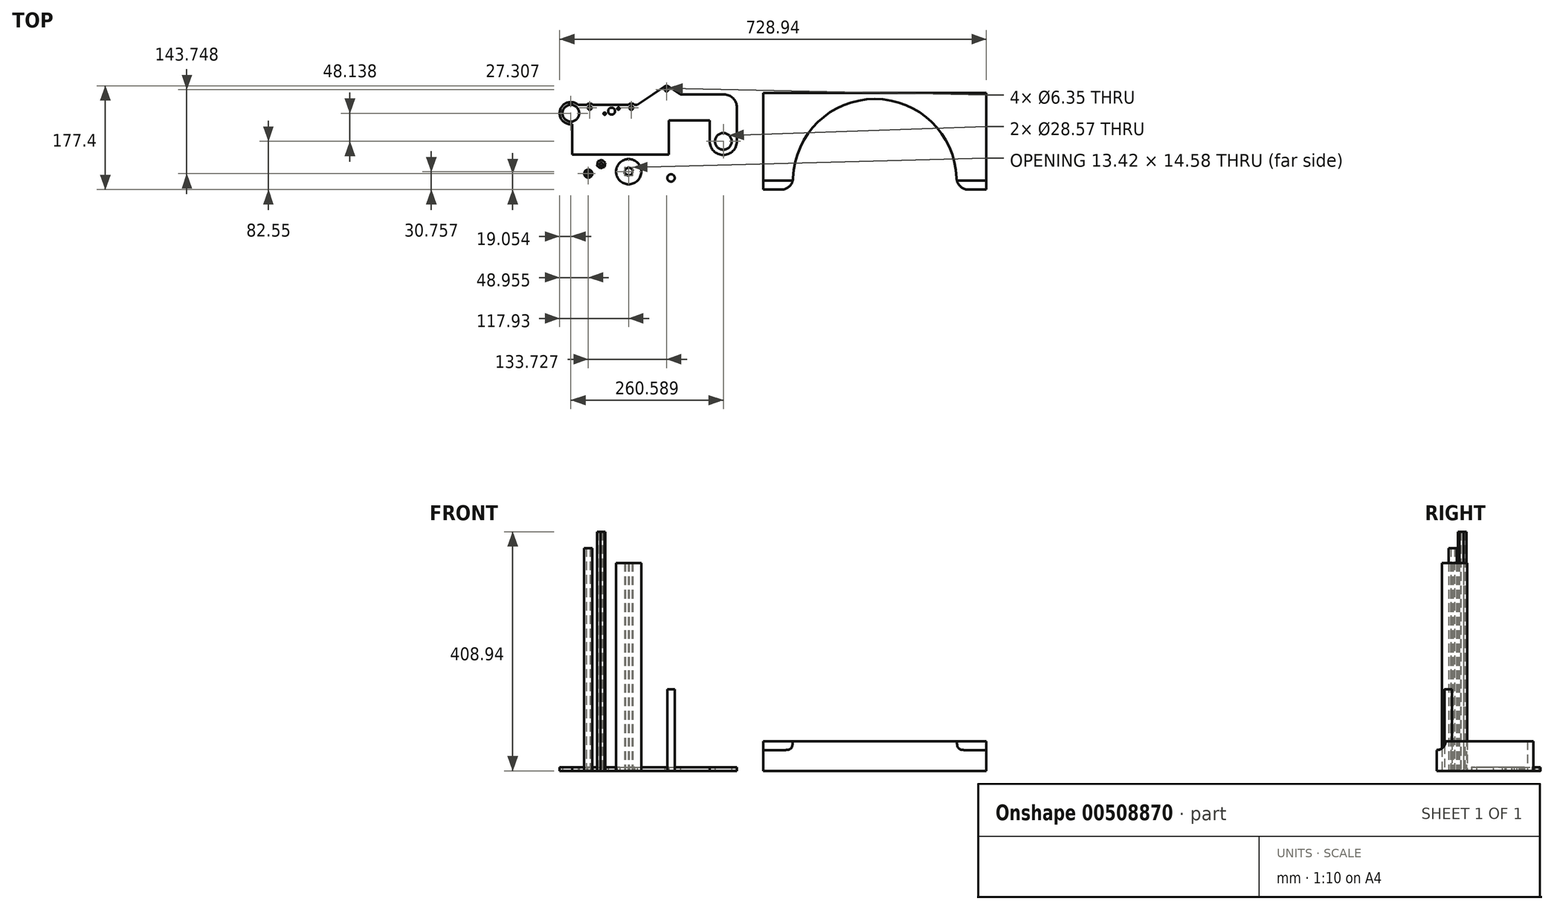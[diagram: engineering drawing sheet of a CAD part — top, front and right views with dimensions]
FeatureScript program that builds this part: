
annotation { "Feature Type Name" : "Feature", "Feature Type Description" : "" }
export const myFeature = defineFeature(function(context is Context, id is Id, definition is map)
    precondition{}
    {
        {
            assignVariable(context, id + "F0", {"name" : "inner_width", "anyValue" : 381 * mm});
        }
        {
            var Q0;
            Q0=qCreatedBy(makeId("Top.planeOp"),FACE);
            var sketch = newSketch(context, id + "F1", { "sketchPlane" : qUnion([Q0])});
            skCircle(sketch, "E0", {"center": v(-76.69, 48.14) * mm, "radius": 21.59 * mm, "construction": true});
            skCircle(sketch, "E1", {"center": v(-76.69, 48.14) * mm, "radius": 14.29 * mm});
            skArc(sketch, "E2", {"start": v(-63.83, 62.2) * mm, "mid": v(-94.85, 53.87) * mm, "end": v(-74.22, 29.25) * mm});
            skLineSegment(sketch, "E3", {"start": v(-74.22, 29.25) * mm, "end": v(-74.22, -22.94) * mm});
            skLineSegment(sketch, "E4", {"start": v(-74.22, -22.94) * mm, "end": v(90.88, -22.94) * mm});
            skLineSegment(sketch, "E5", {"start": v(90.88, -22.94) * mm, "end": v(90.88, 35.73) * mm});
            skLineSegment(sketch, "E6", {"start": v(184.86, 80.18) * mm, "end": v(110.56, 80.18) * mm});
            skLineSegment(sketch, "E7", {"start": v(-74.22, 14.56) * mm, "end": v(90.88, 14.56) * mm, "construction": true});
            skPoint(sketch, "E8.centerSnap0", {"position": v(205.18, 57.96) * mm});
            skArc(sketch, "E9", {"start": v(90.5, 93.76) * mm, "mid": v(86.94, 94.85) * mm, "end": v(83.38, 93.76) * mm});
            skLineSegment(sketch, "E10", {"start": v(83.38, 93.76) * mm, "end": v(63.33, 80.18) * mm});
            skLineSegment(sketch, "E11", {"start": v(90.5, 93.76) * mm, "end": v(110.56, 80.18) * mm});
            skCircle(sketch, "E12", {"center": v(86.94, 88.5) * mm, "radius": 3.18 * mm});
            skLineSegment(sketch, "E13", {"start": v(36.9, 62.2) * mm, "end": v(63.33, 80.18) * mm});
            skCircle(sketch, "E14", {"center": v(-7, 51.68) * mm, "radius": 6 * mm});
            skCircle(sketch, "E15", {"center": v(4.74, 55.96) * mm, "radius": 2 * mm});
            skLineSegment(sketch, "E16", {"start": v(4.74, 55.96) * mm, "end": v(-18.75, 47.4) * mm, "construction": true});
            skCircle(sketch, "E17", {"center": v(-18.75, 47.4) * mm, "radius": 2 * mm});
            skLineSegment(sketch, "E18", {"start": v(-7, 51.68) * mm, "end": v(3.74, 51.68) * mm, "construction": true});
            skCircle(sketch, "E19", {"center": v(-44.31, 57.12) * mm, "radius": 3.18 * mm});
            skCircle(sketch, "E20", {"center": v(26.72, 57.12) * mm, "radius": 3.18 * mm});
            skLineSegment(sketch, "E21", {"start": v(-63.83, 62.2) * mm, "end": v(-50, 62.2) * mm});
            skArc(sketch, "E22", {"start": v(-38.63, 62.2) * mm, "mid": v(-44.31, 64.74) * mm, "end": v(-50, 62.2) * mm});
            skArc(sketch, "E23", {"start": v(32.4, 62.2) * mm, "mid": v(26.72, 64.74) * mm, "end": v(21.04, 62.2) * mm});
            skLineSegment(sketch, "E24.trimOffspring", {"start": v(32.4, 62.2) * mm, "end": v(36.9, 62.2) * mm});
            skLineSegment(sketch, "E25.trimOffspring", {"start": v(-38.63, 62.2) * mm, "end": v(21.04, 62.2) * mm});
            skPoint(sketch, "E26.orphan", {"position": v(205.18, 35.73) * mm});
            skPoint(sketch, "E27.end.orphan", {"position": v(205.18, 80.18) * mm});
            skLineSegment(sketch, "E28", {"start": v(160.73, 35.73) * mm, "end": v(160.73, 0) * mm});
            skArc(sketch, "E29", {"start": v(184.86, 80.18) * mm, "mid": v(200.57, 73.67) * mm, "end": v(207.08, 57.96) * mm});
            skLineSegment(sketch, "E30", {"start": v(207.08, 57.96) * mm, "end": v(207.08, 0) * mm});
            skArc(sketch, "E31", {"start": v(160.73, 0) * mm, "mid": v(183.9, -23.18) * mm, "end": v(207.08, 0) * mm});
            skLineSegment(sketch, "E32", {"start": v(90.88, 35.73) * mm, "end": v(160.73, 35.73) * mm});
            skCircle(sketch, "E33", {"center": v(183.9, 0) * mm, "radius": 14.29 * mm});
            skSolve(sketch);
        }
        {
            var Q0;
            Q0=makeQuery(id+"F1.imprint","IMPRINT",FACE,{"disambiguationData":[TD([[makeQuery(id+"F1.imprint","IMPRINT",EDGE,{"derivedFrom":sQuery(id+"F1.wireOp",EDGE,"E1")}),-1.0]])]});
            var Q1;
            Q1=makeQuery(id+"F1.imprint","IMPRINT",FACE,{"disambiguationData":[TD([[makeQuery(id+"F1.imprint","IMPRINT",EDGE,{"derivedFrom":sQuery(id+"F1.wireOp",EDGE,"E19")}),-1.0]])]});
            var Q2;
            Q2=makeQuery(id+"F1.imprint","IMPRINT",FACE,{"disambiguationData":[TD([[makeQuery(id+"F1.imprint","IMPRINT",EDGE,{"derivedFrom":sQuery(id+"F1.wireOp",EDGE,"E20")}),-1.0]])]});
            extrude(context, id + "F2", {"entities" : qUnion([Q0, Q1, Q2]), "depth" : 6.35 * mm});
        }
        {
            var Q0;
            Q0=qCreatedBy(makeId("Top.planeOp"),FACE);
            var sketch = newSketch(context, id + "F3", { "sketchPlane" : qUnion([Q0])});
            skCircle(sketch, "E34", {"center": v(-46.78, -55.24) * mm, "radius": 6.99 * mm});
            skCircle(sketch, "E35", {"center": v(-46.78, -55.24) * mm, "radius": 3.18 * mm});
            skSolve(sketch);
        }
        {
            var Q0;
            Q0=qSketchRegion(id+"F3",true);
            extrude(context, id + "F4", {"entities" : qUnion([Q0]), "depth" : getVariable(context, 'inner_width')});
        }
        {
            var Q0;
            Q0=qCreatedBy(makeId("Top.planeOp"),FACE);
            var sketch = newSketch(context, id + "F5", { "sketchPlane" : qUnion([Q0])});
            skCircle(sketch, "E36.cCircle", {"center": v(-24.83, -39.03) * mm, "radius": 6.35 * mm, "construction": true});
            skLineSegment(sketch, "E36.0", {"start": v(-19.3, -43.86) * mm, "end": v(-26.24, -46.23) * mm});
            skLineSegment(sketch, "E36.1", {"start": v(-26.24, -46.23) * mm, "end": v(-31.77, -41.4) * mm});
            skLineSegment(sketch, "E36.2", {"start": v(-31.77, -41.4) * mm, "end": v(-30.35, -34.2) * mm});
            skLineSegment(sketch, "E36.3", {"start": v(-30.35, -34.2) * mm, "end": v(-23.4, -31.84) * mm});
            skLineSegment(sketch, "E36.4", {"start": v(-23.4, -31.84) * mm, "end": v(-17.89, -36.66) * mm});
            skLineSegment(sketch, "E36.5", {"start": v(-17.89, -36.66) * mm, "end": v(-19.3, -43.86) * mm});
            skPoint(sketch, "E36.0.midPoint", {"position": v(-22.77, -45.04) * mm});
            skCircle(sketch, "E37", {"center": v(-24.83, -39.03) * mm, "radius": 2.55 * mm});
            skSolve(sketch);
        }
        {
            var Q0;
            Q0=qSketchRegion(id+"F5",true);
            extrude(context, id + "F6", {"entities" : qUnion([Q0]), "depth" : getVariable(context, 'inner_width') + 27.94 * mm});
        }
        {
            var Q0;
            Q0=qCreatedBy(makeId("Top.planeOp"),FACE);
            var sketch = newSketch(context, id + "F7", { "sketchPlane" : qUnion([Q0])});
            skCircle(sketch, "E38", {"center": v(22.2, -51.8) * mm, "radius": 21.59 * mm});
            skCircle(sketch, "E39.cCircle", {"center": v(22.2, -51.8) * mm, "radius": 6.35 * mm, "construction": true});
            skLineSegment(sketch, "E39.0", {"start": v(28.1, -56.12) * mm, "end": v(21.4, -59.08) * mm});
            skLineSegment(sketch, "E39.1", {"start": v(21.4, -59.08) * mm, "end": v(15.48, -54.75) * mm});
            skLineSegment(sketch, "E39.2", {"start": v(15.48, -54.75) * mm, "end": v(16.27, -47.46) * mm});
            skLineSegment(sketch, "E39.3", {"start": v(16.27, -47.46) * mm, "end": v(22.98, -44.5) * mm});
            skLineSegment(sketch, "E39.4", {"start": v(22.98, -44.5) * mm, "end": v(28.9, -48.83) * mm});
            skLineSegment(sketch, "E39.5", {"start": v(28.9, -48.83) * mm, "end": v(28.1, -56.12) * mm});
            skPoint(sketch, "E39.0.midPoint", {"position": v(24.75, -57.6) * mm});
            skSolve(sketch);
        }
        {
            var Q0;
            Q0=makeQuery(id+"F7.imprint","IMPRINT",FACE,{"disambiguationData":[TD([[makeQuery(id+"F7.imprint","IMPRINT",EDGE,{"derivedFrom":sQuery(id+"F7.wireOp",EDGE,"E38")}),1.0]])]});
            extrude(context, id + "F8", {"entities" : qUnion([Q0]), "depth" : getVariable(context, 'inner_width') - 25.4 * mm});
        }
        {
            var Q0;
            Q0=qCreatedBy(makeId("Top.planeOp"),FACE);
            var sketch = newSketch(context, id + "F9", { "sketchPlane" : qUnion([Q0])});
            skLineSegment(sketch, "E40.bottom", {"start": v(252.2, 82.55) * mm, "end": v(633.2, 82.55) * mm});
            skLineSegment(sketch, "E40.top", {"start": v(252.2, -82.55) * mm, "end": v(303.84, -82.55) * mm});
            skLineSegment(sketch, "E40.left", {"start": v(252.2, 82.55) * mm, "end": v(252.2, -82.55) * mm});
            skLineSegment(sketch, "E40.right", {"start": v(633.2, 82.55) * mm, "end": v(633.2, -82.55) * mm});
            skPoint(sketch, "E40.middle", {"position": v(442.7, 0) * mm});
            skArc(sketch, "E41", {"start": v(581.57, -82.55) * mm, "mid": v(442.7, 72.4) * mm, "end": v(303.84, -82.55) * mm});
            skLineSegment(sketch, "E42.trimOffspring", {"start": v(581.57, -82.55) * mm, "end": v(633.2, -82.55) * mm});
            skSolve(sketch);
        }
        {
            var Q0;
            Q0=qSketchRegion(id+"F9",true);
            extrude(context, id + "F10", {"entities" : qUnion([Q0]), "depth" : 50.8 * mm});
        }
        {
            var Q0;
            Q0=makeQuery(id+"F10.opExtrude","SWEPT_EDGE",EDGE,{"disambiguationData":[OSD([sQuery(id+"F9.wireOp",EDGE,"E40.top"),sQuery(id+"F9.wireOp",EDGE,"E41")])]});
            var Q1;
            Q1=makeQuery(id+"F10.opExtrude","SWEPT_EDGE",EDGE,{"disambiguationData":[OSD([sQuery(id+"F9.wireOp",EDGE,"E41"),sQuery(id+"F9.wireOp",EDGE,"E42.trimOffspring")])]});
            fillet(context, id + "F11", {"entities" : qUnion([Q0, Q1]), "radius" : 20.32 * mm, "tangentPropagation" : true, "allowEdgeOverflow" : false});
        }
        {
            var Q0;
            Q0=makeQuery(id+"F10.opExtrude","SWEPT_FACE",FACE,{"disambiguationData":[OSD([sQuery(id+"F9.wireOp",EDGE,"E40.right")])]});
            var sketch = newSketch(context, id + "F12", { "sketchPlane" : qUnion([Q0])});
            skLineSegment(sketch, "E43.0.0", {"start": v(-82.55, 0) * mm, "end": v(82.55, 0) * mm});
            skLineSegment(sketch, "E43.0.1", {"start": v(82.55, 0) * mm, "end": v(82.55, 50.8) * mm});
            skLineSegment(sketch, "E43.0.2", {"start": v(82.55, 50.8) * mm, "end": v(-82.55, 50.8) * mm});
            skLineSegment(sketch, "E43.0.3", {"start": v(-82.55, 50.8) * mm, "end": v(-82.55, 0) * mm});
            skCircle(sketch, "E44", {"center": v(-82.55, 50.8) * mm, "radius": 15.24 * mm});
            skSolve(sketch);
        }
        {
            var Q0;
            {var subQ0=sQuery(id+"F12.wireOp",EDGE,"E43.0.3");var subQ1=sQuery(id+"F12.wireOp",EDGE,"E43.0.2");var subQ2=makeQuery(id+"F12.imprint","INTERSECT",VERTEX,{"derivedFrom":[subQ1,subQ0]});Q0=makeQuery(id+"F12.imprint","IMPRINT",FACE,{"disambiguationData":[TD([[makeQuery(id+"F12.imprint","IMPRINT",EDGE,{"disambiguationData":[TD([[subQ2,1.0]])],"derivedFrom":subQ1}),1.0]])]});}
            var Q1;
            Q1=makeQuery(id+"F10.opExtrude","SWEPT_FACE",FACE,{"disambiguationData":[OSD([sQuery(id+"F9.wireOp",EDGE,"E40.left")])]});
            extrude(context, id + "F13", {"entities" : qUnion([Q0]), "operationType" : NewBodyOperationType.REMOVE, "endBound" : BoundingType.UP_TO_SURFACE, "oppositeDirection" : true, "endBoundEntityFace" : qUnion([Q1]), "depth" : 25.4 * mm});
        }
        {
            var Q0;
            Q0=qCreatedBy(makeId("Top.planeOp"),FACE);
            var sketch = newSketch(context, id + "F14", { "sketchPlane" : qUnion([Q0])});
            skCircle(sketch, "E45", {"center": v(94.46, -62.59) * mm, "radius": 6.35 * mm});
            skSolve(sketch);
        }
        {
            var Q0;
            Q0=qSketchRegion(id+"F14",true);
            extrude(context, id + "F15", {"entities" : qUnion([Q0]), "depth" : 139.7 * mm});
        }
    });
